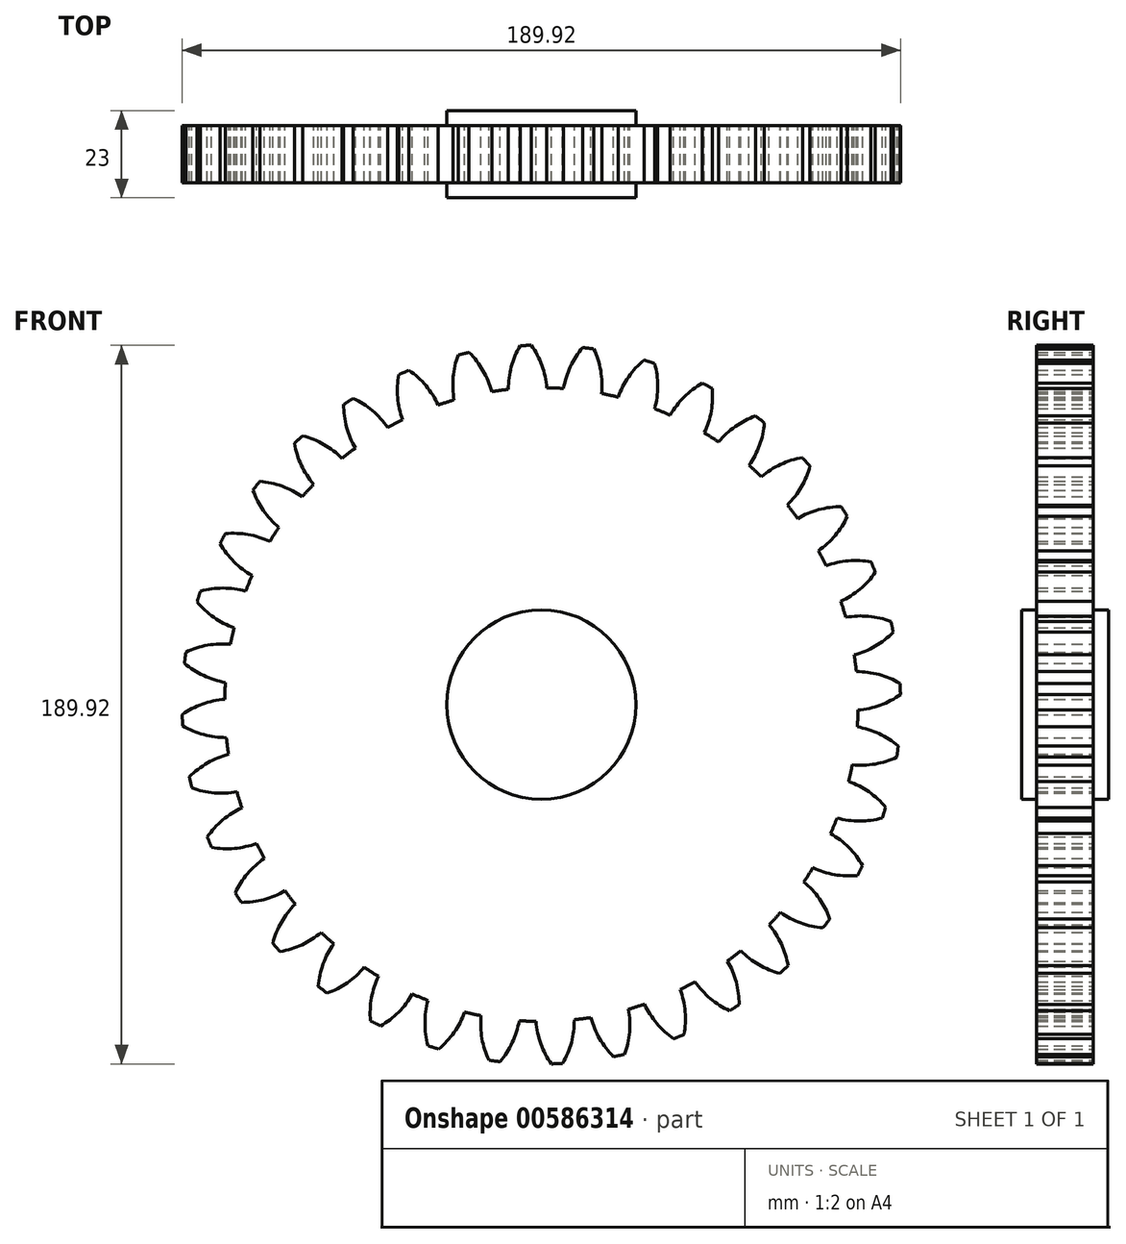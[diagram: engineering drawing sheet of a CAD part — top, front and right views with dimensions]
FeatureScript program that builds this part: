
annotation { "Feature Type Name" : "Feature", "Feature Type Description" : "" }
export const myFeature = defineFeature(function(context is Context, id is Id, definition is map)
    precondition{}
    {
        {
            var Q0;
            Q0=qCreatedBy(makeId("Front.planeOp"),FACE);
            var sketch = newSketch(context, id + "F0", { "sketchPlane" : qUnion([Q0])});
            skCircle(sketch, "E0", {"center": v(0, 0) * mm, "radius": 83.75 * mm});
            skCircle(sketch, "E1", {"center": v(0, 0) * mm, "radius": 90 * mm, "construction": true});
            skCircle(sketch, "E2", {"center": v(0, 0) * mm, "radius": 95 * mm, "construction": true});
            skLineSegment(sketch, "E3", {"start": v(0, 0) * mm, "end": v(0, 175.5) * mm, "construction": true});
            skLineSegment(sketch, "E4", {"start": v(0, 0) * mm, "end": v(-7.83, 179.33) * mm, "construction": true});
            skLineSegment(sketch, "E5", {"start": v(0, 90) * mm, "end": v(-217.65, 90) * mm, "construction": true});
            skLineSegment(sketch, "E6", {"start": v(0, 90) * mm, "end": v(-200.71, 16.95) * mm, "construction": true});
            skCircle(sketch, "E7", {"center": v(0, 0) * mm, "radius": 84.57 * mm, "construction": true});
            skCircle(sketch, "E8", {"center": v(0, 90) * mm, "radius": 22.5 * mm, "construction": true});
            skArc(sketch, "E9", {"start": v(0, 90) * mm, "mid": v(-1.18, 92.57) * mm, "end": v(-2.66, 94.96) * mm});
            skArc(sketch, "E10", {"start": v(1.43, 83.74) * mm, "mid": v(0.94, 86.92) * mm, "end": v(0, 90) * mm});
            skArc(sketch, "E11.MirrorCS", {"start": v(-8.72, 83.3) * mm, "mid": v(-8.5, 86.5) * mm, "end": v(-7.84, 89.66) * mm});
            skArc(sketch, "E12.MirrorCS", {"start": v(-7.84, 89.66) * mm, "mid": v(-6.9, 92.32) * mm, "end": v(-5.62, 94.83) * mm});
            skArc(sketch, "E13", {"start": v(-5.62, 94.83) * mm, "mid": v(-4.14, 94.9) * mm, "end": v(-2.66, 94.96) * mm});
            skCircle(sketch, "E14", {"center": v(0, 0) * mm, "radius": 25 * mm});
            skSolve(sketch);
        }
        {
            var Q0;
            Q0=makeQuery(id+"F0.imprint","IMPRINT",FACE,{"disambiguationData":[TD([[makeQuery(id+"F0.imprint","IMPRINT",EDGE,{"derivedFrom":sQuery(id+"F0.wireOp",EDGE,"E9")}),1.0]])]});
            var Q1;
            {var subQ0=sQuery(id+"F0.wireOp",EDGE,"E0");var subQ1=makeQuery(id+"F0.imprint","INTERSECT",VERTEX,{"derivedFrom":[subQ0,sQuery(id+"F0.wireOp",EDGE,"E10")]});Q1=makeQuery(id+"F0.imprint","IMPRINT",FACE,{"disambiguationData":[TD([[makeQuery(id+"F0.imprint","IMPRINT",EDGE,{"disambiguationData":[TD([[subQ1,-1.0]])],"derivedFrom":subQ0}),1.0]])]});}
            var Q2;
            Q2=makeQuery(id+"F0.imprint","IMPRINT",FACE,{"disambiguationData":[TD([[makeQuery(id+"F0.imprint","IMPRINT",EDGE,{"derivedFrom":sQuery(id+"F0.wireOp",EDGE,"E14")}),1.0]])]});
            extrude(context, id + "F1", {"entities" : qUnion([Q0, Q1, Q2]), "depth" : 15 * mm, "offsetDistance" : 25.4 * mm});
        }
        {
            var Q0;
            Q0=makeQuery(id+"F1.opExtrude","SWEPT_BODY",BODY,{"disambiguationData":[OSD([sQuery(id+"F0.wireOp",EDGE,"E0"),sQuery(id+"F0.wireOp",EDGE,"E9"),sQuery(id+"F0.wireOp",EDGE,"E10"),sQuery(id+"F0.wireOp",EDGE,"E11.MirrorCS"),sQuery(id+"F0.wireOp",EDGE,"E12.MirrorCS"),sQuery(id+"F0.wireOp",EDGE,"E13")])]});
            var Q1;
            Q1=makeQuery(id+"F1.opExtrude","SWEPT_FACE",FACE,{"disambiguationData":[OSD([sQuery(id+"F0.wireOp",EDGE,"E0")])]});
            circularPattern(context, id + "F2", {"entities" : qUnion([Q0]), "axis" : qUnion([Q1]), "angle" : 360 * degree, "instanceCount" : 36, "equalSpace" : true});
        }
        {
            var Q0;
            Q0=makeQuery(id+"F2.opPattern","COPY",BODY,{"derivedFrom":makeQuery(id+"F1.opExtrude","SWEPT_BODY",BODY,{"disambiguationData":[OSD([sQuery(id+"F0.wireOp",EDGE,"E0"),sQuery(id+"F0.wireOp",EDGE,"E9"),sQuery(id+"F0.wireOp",EDGE,"E10"),sQuery(id+"F0.wireOp",EDGE,"E11.MirrorCS"),sQuery(id+"F0.wireOp",EDGE,"E12.MirrorCS"),sQuery(id+"F0.wireOp",EDGE,"E13")])]}),"instanceName":"11"});
            var Q1;
            Q1=makeQuery(id+"F2.opPattern","COPY",BODY,{"derivedFrom":makeQuery(id+"F1.opExtrude","SWEPT_BODY",BODY,{"disambiguationData":[OSD([sQuery(id+"F0.wireOp",EDGE,"E0"),sQuery(id+"F0.wireOp",EDGE,"E9"),sQuery(id+"F0.wireOp",EDGE,"E10"),sQuery(id+"F0.wireOp",EDGE,"E11.MirrorCS"),sQuery(id+"F0.wireOp",EDGE,"E12.MirrorCS"),sQuery(id+"F0.wireOp",EDGE,"E13")])]}),"instanceName":"1"});
            var Q2;
            Q2=makeQuery(id+"F2.opPattern","COPY",BODY,{"derivedFrom":makeQuery(id+"F1.opExtrude","SWEPT_BODY",BODY,{"disambiguationData":[OSD([sQuery(id+"F0.wireOp",EDGE,"E0"),sQuery(id+"F0.wireOp",EDGE,"E9"),sQuery(id+"F0.wireOp",EDGE,"E10"),sQuery(id+"F0.wireOp",EDGE,"E11.MirrorCS"),sQuery(id+"F0.wireOp",EDGE,"E12.MirrorCS"),sQuery(id+"F0.wireOp",EDGE,"E13")])]}),"instanceName":"22"});
            var Q3;
            Q3=makeQuery(id+"F2.opPattern","COPY",BODY,{"derivedFrom":makeQuery(id+"F1.opExtrude","SWEPT_BODY",BODY,{"disambiguationData":[OSD([sQuery(id+"F0.wireOp",EDGE,"E0"),sQuery(id+"F0.wireOp",EDGE,"E9"),sQuery(id+"F0.wireOp",EDGE,"E10"),sQuery(id+"F0.wireOp",EDGE,"E11.MirrorCS"),sQuery(id+"F0.wireOp",EDGE,"E12.MirrorCS"),sQuery(id+"F0.wireOp",EDGE,"E13")])]}),"instanceName":"28"});
            var Q4;
            Q4=makeQuery(id+"F2.opPattern","COPY",BODY,{"derivedFrom":makeQuery(id+"F1.opExtrude","SWEPT_BODY",BODY,{"disambiguationData":[OSD([sQuery(id+"F0.wireOp",EDGE,"E0"),sQuery(id+"F0.wireOp",EDGE,"E9"),sQuery(id+"F0.wireOp",EDGE,"E10"),sQuery(id+"F0.wireOp",EDGE,"E11.MirrorCS"),sQuery(id+"F0.wireOp",EDGE,"E12.MirrorCS"),sQuery(id+"F0.wireOp",EDGE,"E13")])]}),"instanceName":"32"});
            var Q5;
            Q5=makeQuery(id+"F2.opPattern","COPY",BODY,{"derivedFrom":makeQuery(id+"F1.opExtrude","SWEPT_BODY",BODY,{"disambiguationData":[OSD([sQuery(id+"F0.wireOp",EDGE,"E0"),sQuery(id+"F0.wireOp",EDGE,"E9"),sQuery(id+"F0.wireOp",EDGE,"E10"),sQuery(id+"F0.wireOp",EDGE,"E11.MirrorCS"),sQuery(id+"F0.wireOp",EDGE,"E12.MirrorCS"),sQuery(id+"F0.wireOp",EDGE,"E13")])]}),"instanceName":"31"});
            var Q6;
            Q6=makeQuery(id+"F2.opPattern","COPY",BODY,{"derivedFrom":makeQuery(id+"F1.opExtrude","SWEPT_BODY",BODY,{"disambiguationData":[OSD([sQuery(id+"F0.wireOp",EDGE,"E0"),sQuery(id+"F0.wireOp",EDGE,"E9"),sQuery(id+"F0.wireOp",EDGE,"E10"),sQuery(id+"F0.wireOp",EDGE,"E11.MirrorCS"),sQuery(id+"F0.wireOp",EDGE,"E12.MirrorCS"),sQuery(id+"F0.wireOp",EDGE,"E13")])]}),"instanceName":"10"});
            var Q7;
            Q7=makeQuery(id+"F2.opPattern","COPY",BODY,{"derivedFrom":makeQuery(id+"F1.opExtrude","SWEPT_BODY",BODY,{"disambiguationData":[OSD([sQuery(id+"F0.wireOp",EDGE,"E0"),sQuery(id+"F0.wireOp",EDGE,"E9"),sQuery(id+"F0.wireOp",EDGE,"E10"),sQuery(id+"F0.wireOp",EDGE,"E11.MirrorCS"),sQuery(id+"F0.wireOp",EDGE,"E12.MirrorCS"),sQuery(id+"F0.wireOp",EDGE,"E13")])]}),"instanceName":"17"});
            var Q8;
            Q8=makeQuery(id+"F2.opPattern","COPY",BODY,{"derivedFrom":makeQuery(id+"F1.opExtrude","SWEPT_BODY",BODY,{"disambiguationData":[OSD([sQuery(id+"F0.wireOp",EDGE,"E0"),sQuery(id+"F0.wireOp",EDGE,"E9"),sQuery(id+"F0.wireOp",EDGE,"E10"),sQuery(id+"F0.wireOp",EDGE,"E11.MirrorCS"),sQuery(id+"F0.wireOp",EDGE,"E12.MirrorCS"),sQuery(id+"F0.wireOp",EDGE,"E13")])]}),"instanceName":"23"});
            var Q9;
            Q9=makeQuery(id+"F2.opPattern","COPY",BODY,{"derivedFrom":makeQuery(id+"F1.opExtrude","SWEPT_BODY",BODY,{"disambiguationData":[OSD([sQuery(id+"F0.wireOp",EDGE,"E0"),sQuery(id+"F0.wireOp",EDGE,"E9"),sQuery(id+"F0.wireOp",EDGE,"E10"),sQuery(id+"F0.wireOp",EDGE,"E11.MirrorCS"),sQuery(id+"F0.wireOp",EDGE,"E12.MirrorCS"),sQuery(id+"F0.wireOp",EDGE,"E13")])]}),"instanceName":"18"});
            var Q10;
            Q10=makeQuery(id+"F2.opPattern","COPY",BODY,{"derivedFrom":makeQuery(id+"F1.opExtrude","SWEPT_BODY",BODY,{"disambiguationData":[OSD([sQuery(id+"F0.wireOp",EDGE,"E0"),sQuery(id+"F0.wireOp",EDGE,"E9"),sQuery(id+"F0.wireOp",EDGE,"E10"),sQuery(id+"F0.wireOp",EDGE,"E11.MirrorCS"),sQuery(id+"F0.wireOp",EDGE,"E12.MirrorCS"),sQuery(id+"F0.wireOp",EDGE,"E13")])]}),"instanceName":"29"});
            var Q11;
            Q11=makeQuery(id+"F2.opPattern","COPY",BODY,{"derivedFrom":makeQuery(id+"F1.opExtrude","SWEPT_BODY",BODY,{"disambiguationData":[OSD([sQuery(id+"F0.wireOp",EDGE,"E0"),sQuery(id+"F0.wireOp",EDGE,"E9"),sQuery(id+"F0.wireOp",EDGE,"E10"),sQuery(id+"F0.wireOp",EDGE,"E11.MirrorCS"),sQuery(id+"F0.wireOp",EDGE,"E12.MirrorCS"),sQuery(id+"F0.wireOp",EDGE,"E13")])]}),"instanceName":"30"});
            var Q12;
            Q12=makeQuery(id+"F2.opPattern","COPY",BODY,{"derivedFrom":makeQuery(id+"F1.opExtrude","SWEPT_BODY",BODY,{"disambiguationData":[OSD([sQuery(id+"F0.wireOp",EDGE,"E0"),sQuery(id+"F0.wireOp",EDGE,"E9"),sQuery(id+"F0.wireOp",EDGE,"E10"),sQuery(id+"F0.wireOp",EDGE,"E11.MirrorCS"),sQuery(id+"F0.wireOp",EDGE,"E12.MirrorCS"),sQuery(id+"F0.wireOp",EDGE,"E13")])]}),"instanceName":"15"});
            var Q13;
            Q13=makeQuery(id+"F2.opPattern","COPY",BODY,{"derivedFrom":makeQuery(id+"F1.opExtrude","SWEPT_BODY",BODY,{"disambiguationData":[OSD([sQuery(id+"F0.wireOp",EDGE,"E0"),sQuery(id+"F0.wireOp",EDGE,"E9"),sQuery(id+"F0.wireOp",EDGE,"E10"),sQuery(id+"F0.wireOp",EDGE,"E11.MirrorCS"),sQuery(id+"F0.wireOp",EDGE,"E12.MirrorCS"),sQuery(id+"F0.wireOp",EDGE,"E13")])]}),"instanceName":"33"});
            var Q14;
            Q14=makeQuery(id+"F2.opPattern","COPY",BODY,{"derivedFrom":makeQuery(id+"F1.opExtrude","SWEPT_BODY",BODY,{"disambiguationData":[OSD([sQuery(id+"F0.wireOp",EDGE,"E0"),sQuery(id+"F0.wireOp",EDGE,"E9"),sQuery(id+"F0.wireOp",EDGE,"E10"),sQuery(id+"F0.wireOp",EDGE,"E11.MirrorCS"),sQuery(id+"F0.wireOp",EDGE,"E12.MirrorCS"),sQuery(id+"F0.wireOp",EDGE,"E13")])]}),"instanceName":"12"});
            var Q15;
            Q15=makeQuery(id+"F2.opPattern","COPY",BODY,{"derivedFrom":makeQuery(id+"F1.opExtrude","SWEPT_BODY",BODY,{"disambiguationData":[OSD([sQuery(id+"F0.wireOp",EDGE,"E0"),sQuery(id+"F0.wireOp",EDGE,"E9"),sQuery(id+"F0.wireOp",EDGE,"E10"),sQuery(id+"F0.wireOp",EDGE,"E11.MirrorCS"),sQuery(id+"F0.wireOp",EDGE,"E12.MirrorCS"),sQuery(id+"F0.wireOp",EDGE,"E13")])]}),"instanceName":"21"});
            var Q16;
            Q16=makeQuery(id+"F2.opPattern","COPY",BODY,{"derivedFrom":makeQuery(id+"F1.opExtrude","SWEPT_BODY",BODY,{"disambiguationData":[OSD([sQuery(id+"F0.wireOp",EDGE,"E0"),sQuery(id+"F0.wireOp",EDGE,"E9"),sQuery(id+"F0.wireOp",EDGE,"E10"),sQuery(id+"F0.wireOp",EDGE,"E11.MirrorCS"),sQuery(id+"F0.wireOp",EDGE,"E12.MirrorCS"),sQuery(id+"F0.wireOp",EDGE,"E13")])]}),"instanceName":"34"});
            var Q17;
            Q17=makeQuery(id+"F2.opPattern","COPY",BODY,{"derivedFrom":makeQuery(id+"F1.opExtrude","SWEPT_BODY",BODY,{"disambiguationData":[OSD([sQuery(id+"F0.wireOp",EDGE,"E0"),sQuery(id+"F0.wireOp",EDGE,"E9"),sQuery(id+"F0.wireOp",EDGE,"E10"),sQuery(id+"F0.wireOp",EDGE,"E11.MirrorCS"),sQuery(id+"F0.wireOp",EDGE,"E12.MirrorCS"),sQuery(id+"F0.wireOp",EDGE,"E13")])]}),"instanceName":"16"});
            var Q18;
            Q18=makeQuery(id+"F1.opExtrude","SWEPT_BODY",BODY,{"disambiguationData":[OSD([sQuery(id+"F0.wireOp",EDGE,"E0"),sQuery(id+"F0.wireOp",EDGE,"E9"),sQuery(id+"F0.wireOp",EDGE,"E10"),sQuery(id+"F0.wireOp",EDGE,"E11.MirrorCS"),sQuery(id+"F0.wireOp",EDGE,"E12.MirrorCS"),sQuery(id+"F0.wireOp",EDGE,"E13")])]});
            var Q19;
            Q19=makeQuery(id+"F2.opPattern","COPY",BODY,{"derivedFrom":makeQuery(id+"F1.opExtrude","SWEPT_BODY",BODY,{"disambiguationData":[OSD([sQuery(id+"F0.wireOp",EDGE,"E0"),sQuery(id+"F0.wireOp",EDGE,"E9"),sQuery(id+"F0.wireOp",EDGE,"E10"),sQuery(id+"F0.wireOp",EDGE,"E11.MirrorCS"),sQuery(id+"F0.wireOp",EDGE,"E12.MirrorCS"),sQuery(id+"F0.wireOp",EDGE,"E13")])]}),"instanceName":"24"});
            var Q20;
            Q20=makeQuery(id+"F2.opPattern","COPY",BODY,{"derivedFrom":makeQuery(id+"F1.opExtrude","SWEPT_BODY",BODY,{"disambiguationData":[OSD([sQuery(id+"F0.wireOp",EDGE,"E0"),sQuery(id+"F0.wireOp",EDGE,"E9"),sQuery(id+"F0.wireOp",EDGE,"E10"),sQuery(id+"F0.wireOp",EDGE,"E11.MirrorCS"),sQuery(id+"F0.wireOp",EDGE,"E12.MirrorCS"),sQuery(id+"F0.wireOp",EDGE,"E13")])]}),"instanceName":"27"});
            var Q21;
            Q21=makeQuery(id+"F2.opPattern","COPY",BODY,{"derivedFrom":makeQuery(id+"F1.opExtrude","SWEPT_BODY",BODY,{"disambiguationData":[OSD([sQuery(id+"F0.wireOp",EDGE,"E0"),sQuery(id+"F0.wireOp",EDGE,"E9"),sQuery(id+"F0.wireOp",EDGE,"E10"),sQuery(id+"F0.wireOp",EDGE,"E11.MirrorCS"),sQuery(id+"F0.wireOp",EDGE,"E12.MirrorCS"),sQuery(id+"F0.wireOp",EDGE,"E13")])]}),"instanceName":"20"});
            var Q22;
            Q22=makeQuery(id+"F2.opPattern","COPY",BODY,{"derivedFrom":makeQuery(id+"F1.opExtrude","SWEPT_BODY",BODY,{"disambiguationData":[OSD([sQuery(id+"F0.wireOp",EDGE,"E0"),sQuery(id+"F0.wireOp",EDGE,"E9"),sQuery(id+"F0.wireOp",EDGE,"E10"),sQuery(id+"F0.wireOp",EDGE,"E11.MirrorCS"),sQuery(id+"F0.wireOp",EDGE,"E12.MirrorCS"),sQuery(id+"F0.wireOp",EDGE,"E13")])]}),"instanceName":"14"});
            var Q23;
            Q23=makeQuery(id+"F2.opPattern","COPY",BODY,{"derivedFrom":makeQuery(id+"F1.opExtrude","SWEPT_BODY",BODY,{"disambiguationData":[OSD([sQuery(id+"F0.wireOp",EDGE,"E0"),sQuery(id+"F0.wireOp",EDGE,"E9"),sQuery(id+"F0.wireOp",EDGE,"E10"),sQuery(id+"F0.wireOp",EDGE,"E11.MirrorCS"),sQuery(id+"F0.wireOp",EDGE,"E12.MirrorCS"),sQuery(id+"F0.wireOp",EDGE,"E13")])]}),"instanceName":"25"});
            var Q24;
            Q24=makeQuery(id+"F2.opPattern","COPY",BODY,{"derivedFrom":makeQuery(id+"F1.opExtrude","SWEPT_BODY",BODY,{"disambiguationData":[OSD([sQuery(id+"F0.wireOp",EDGE,"E0"),sQuery(id+"F0.wireOp",EDGE,"E9"),sQuery(id+"F0.wireOp",EDGE,"E10"),sQuery(id+"F0.wireOp",EDGE,"E11.MirrorCS"),sQuery(id+"F0.wireOp",EDGE,"E12.MirrorCS"),sQuery(id+"F0.wireOp",EDGE,"E13")])]}),"instanceName":"26"});
            var Q25;
            Q25=makeQuery(id+"F2.opPattern","COPY",BODY,{"derivedFrom":makeQuery(id+"F1.opExtrude","SWEPT_BODY",BODY,{"disambiguationData":[OSD([sQuery(id+"F0.wireOp",EDGE,"E0"),sQuery(id+"F0.wireOp",EDGE,"E9"),sQuery(id+"F0.wireOp",EDGE,"E10"),sQuery(id+"F0.wireOp",EDGE,"E11.MirrorCS"),sQuery(id+"F0.wireOp",EDGE,"E12.MirrorCS"),sQuery(id+"F0.wireOp",EDGE,"E13")])]}),"instanceName":"35"});
            var Q26;
            Q26=makeQuery(id+"F2.opPattern","COPY",BODY,{"derivedFrom":makeQuery(id+"F1.opExtrude","SWEPT_BODY",BODY,{"disambiguationData":[OSD([sQuery(id+"F0.wireOp",EDGE,"E0"),sQuery(id+"F0.wireOp",EDGE,"E9"),sQuery(id+"F0.wireOp",EDGE,"E10"),sQuery(id+"F0.wireOp",EDGE,"E11.MirrorCS"),sQuery(id+"F0.wireOp",EDGE,"E12.MirrorCS"),sQuery(id+"F0.wireOp",EDGE,"E13")])]}),"instanceName":"9"});
            var Q27;
            Q27=makeQuery(id+"F2.opPattern","COPY",BODY,{"derivedFrom":makeQuery(id+"F1.opExtrude","SWEPT_BODY",BODY,{"disambiguationData":[OSD([sQuery(id+"F0.wireOp",EDGE,"E0"),sQuery(id+"F0.wireOp",EDGE,"E9"),sQuery(id+"F0.wireOp",EDGE,"E10"),sQuery(id+"F0.wireOp",EDGE,"E11.MirrorCS"),sQuery(id+"F0.wireOp",EDGE,"E12.MirrorCS"),sQuery(id+"F0.wireOp",EDGE,"E13")])]}),"instanceName":"19"});
            var Q28;
            Q28=makeQuery(id+"F2.opPattern","COPY",BODY,{"derivedFrom":makeQuery(id+"F1.opExtrude","SWEPT_BODY",BODY,{"disambiguationData":[OSD([sQuery(id+"F0.wireOp",EDGE,"E0"),sQuery(id+"F0.wireOp",EDGE,"E9"),sQuery(id+"F0.wireOp",EDGE,"E10"),sQuery(id+"F0.wireOp",EDGE,"E11.MirrorCS"),sQuery(id+"F0.wireOp",EDGE,"E12.MirrorCS"),sQuery(id+"F0.wireOp",EDGE,"E13")])]}),"instanceName":"6"});
            var Q29;
            Q29=makeQuery(id+"F2.opPattern","COPY",BODY,{"derivedFrom":makeQuery(id+"F1.opExtrude","SWEPT_BODY",BODY,{"disambiguationData":[OSD([sQuery(id+"F0.wireOp",EDGE,"E0"),sQuery(id+"F0.wireOp",EDGE,"E9"),sQuery(id+"F0.wireOp",EDGE,"E10"),sQuery(id+"F0.wireOp",EDGE,"E11.MirrorCS"),sQuery(id+"F0.wireOp",EDGE,"E12.MirrorCS"),sQuery(id+"F0.wireOp",EDGE,"E13")])]}),"instanceName":"3"});
            var Q30;
            Q30=makeQuery(id+"F2.opPattern","COPY",BODY,{"derivedFrom":makeQuery(id+"F1.opExtrude","SWEPT_BODY",BODY,{"disambiguationData":[OSD([sQuery(id+"F0.wireOp",EDGE,"E0"),sQuery(id+"F0.wireOp",EDGE,"E9"),sQuery(id+"F0.wireOp",EDGE,"E10"),sQuery(id+"F0.wireOp",EDGE,"E11.MirrorCS"),sQuery(id+"F0.wireOp",EDGE,"E12.MirrorCS"),sQuery(id+"F0.wireOp",EDGE,"E13")])]}),"instanceName":"13"});
            var Q31;
            Q31=makeQuery(id+"F2.opPattern","COPY",BODY,{"derivedFrom":makeQuery(id+"F1.opExtrude","SWEPT_BODY",BODY,{"disambiguationData":[OSD([sQuery(id+"F0.wireOp",EDGE,"E0"),sQuery(id+"F0.wireOp",EDGE,"E9"),sQuery(id+"F0.wireOp",EDGE,"E10"),sQuery(id+"F0.wireOp",EDGE,"E11.MirrorCS"),sQuery(id+"F0.wireOp",EDGE,"E12.MirrorCS"),sQuery(id+"F0.wireOp",EDGE,"E13")])]}),"instanceName":"7"});
            var Q32;
            Q32=makeQuery(id+"F2.opPattern","COPY",BODY,{"derivedFrom":makeQuery(id+"F1.opExtrude","SWEPT_BODY",BODY,{"disambiguationData":[OSD([sQuery(id+"F0.wireOp",EDGE,"E0"),sQuery(id+"F0.wireOp",EDGE,"E9"),sQuery(id+"F0.wireOp",EDGE,"E10"),sQuery(id+"F0.wireOp",EDGE,"E11.MirrorCS"),sQuery(id+"F0.wireOp",EDGE,"E12.MirrorCS"),sQuery(id+"F0.wireOp",EDGE,"E13")])]}),"instanceName":"5"});
            var Q33;
            Q33=makeQuery(id+"F2.opPattern","COPY",BODY,{"derivedFrom":makeQuery(id+"F1.opExtrude","SWEPT_BODY",BODY,{"disambiguationData":[OSD([sQuery(id+"F0.wireOp",EDGE,"E0"),sQuery(id+"F0.wireOp",EDGE,"E9"),sQuery(id+"F0.wireOp",EDGE,"E10"),sQuery(id+"F0.wireOp",EDGE,"E11.MirrorCS"),sQuery(id+"F0.wireOp",EDGE,"E12.MirrorCS"),sQuery(id+"F0.wireOp",EDGE,"E13")])]}),"instanceName":"8"});
            var Q34;
            Q34=makeQuery(id+"F2.opPattern","COPY",BODY,{"derivedFrom":makeQuery(id+"F1.opExtrude","SWEPT_BODY",BODY,{"disambiguationData":[OSD([sQuery(id+"F0.wireOp",EDGE,"E0"),sQuery(id+"F0.wireOp",EDGE,"E9"),sQuery(id+"F0.wireOp",EDGE,"E10"),sQuery(id+"F0.wireOp",EDGE,"E11.MirrorCS"),sQuery(id+"F0.wireOp",EDGE,"E12.MirrorCS"),sQuery(id+"F0.wireOp",EDGE,"E13")])]}),"instanceName":"4"});
            var Q35;
            Q35=makeQuery(id+"F2.opPattern","COPY",BODY,{"derivedFrom":makeQuery(id+"F1.opExtrude","SWEPT_BODY",BODY,{"disambiguationData":[OSD([sQuery(id+"F0.wireOp",EDGE,"E0"),sQuery(id+"F0.wireOp",EDGE,"E9"),sQuery(id+"F0.wireOp",EDGE,"E10"),sQuery(id+"F0.wireOp",EDGE,"E11.MirrorCS"),sQuery(id+"F0.wireOp",EDGE,"E12.MirrorCS"),sQuery(id+"F0.wireOp",EDGE,"E13")])]}),"instanceName":"2"});
            booleanBodies(context, id + "F3", {"operationType" : BooleanOperationType.UNION, "tools" : qUnion([Q0, Q1, Q2, Q3, Q4, Q5, Q6, Q7, Q8, Q9, Q10, Q11, Q12, Q13, Q14, Q15, Q16, Q17, Q18, Q19, Q20, Q21, Q22, Q23, Q24, Q25, Q26, Q27, Q28, Q29, Q30, Q31, Q32, Q33, Q34, Q35])});
        }
        {
            var Q0;
            Q0=makeQuery(id+"F0.imprint","IMPRINT",FACE,{"disambiguationData":[TD([[makeQuery(id+"F0.imprint","IMPRINT",EDGE,{"derivedFrom":sQuery(id+"F0.wireOp",EDGE,"E14")}),1.0]])]});
            extrude(context, id + "F4", {"entities" : qUnion([Q0]), "operationType" : NewBodyOperationType.ADD, "oppositeDirection" : true, "depth" : 4 * mm, "offsetDistance" : 25.4 * mm});
        }
        {
            var Q0;
            Q0=makeQuery(id+"F4.opExtrude","CAP_FACE",FACE,{"disambiguationData":[OSD([sQuery(id+"F0.wireOp",EDGE,"E14")])],"isStart":false});
            extrude(context, id + "F5", {"entities" : qUnion([Q0]), "operationType" : NewBodyOperationType.ADD, "oppositeDirection" : true, "depth" : 23 * mm, "offsetDistance" : 25.4 * mm});
        }
    });
